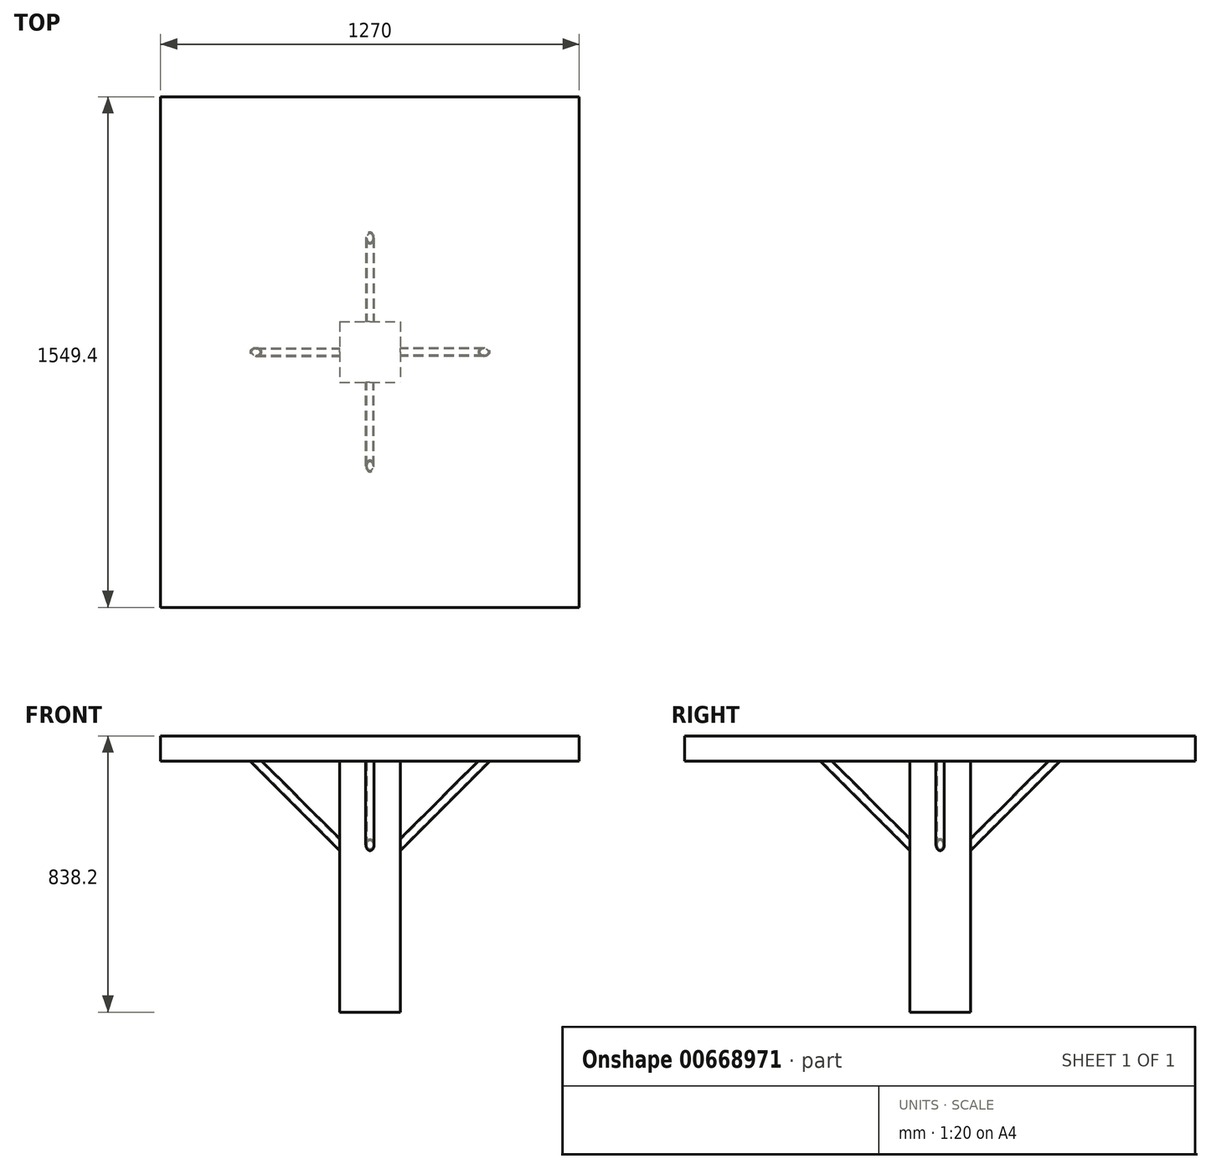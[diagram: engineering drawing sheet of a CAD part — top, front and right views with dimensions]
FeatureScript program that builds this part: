
annotation { "Feature Type Name" : "Feature", "Feature Type Description" : "" }
export const myFeature = defineFeature(function(context is Context, id is Id, definition is map)
    precondition{}
    {
        {
            var Q0;
            Q0=qCreatedBy(makeId("Top.planeOp"),FACE);
            var sketch = newSketch(context, id + "F0", { "sketchPlane" : qUnion([Q0])});
            skLineSegment(sketch, "E0.bottom", {"start": v(-92.08, 92.08) * mm, "end": v(92.08, 92.08) * mm});
            skLineSegment(sketch, "E0.top", {"start": v(-92.08, -92.08) * mm, "end": v(92.08, -92.08) * mm});
            skLineSegment(sketch, "E0.left", {"start": v(-92.08, 92.08) * mm, "end": v(-92.08, -92.08) * mm});
            skLineSegment(sketch, "E0.right", {"start": v(92.08, 92.08) * mm, "end": v(92.08, -92.08) * mm});
            skSolve(sketch);
        }
        {
            var Q0;
            Q0 = qSketchRegion(id + "F0", true);
            extrude(context, id + "F1", {"entities" : qUnion([Q0]), "depth" : 762 * mm, "offsetDistance" : 25.4 * mm});
        }
        {
            var Q0;
            Q0=qCreatedBy(makeId("Front.planeOp"),FACE);
            var sketch = newSketch(context, id + "F2", { "sketchPlane" : qUnion([Q0])});
            skLineSegment(sketch, "E1", {"start": v(0, 1153.25) * mm, "end": v(0, 0) * mm});
            skSolve(sketch);
        }
        {
            var Q0;
            Q0=makeQuery(id+"F1.opExtrude","SWEPT_FACE",FACE,{"disambiguationData":[OSD([sQuery(id+"F0.wireOp",EDGE,"E0.left")])]});
            var sketch = newSketch(context, id + "F3", { "sketchPlane" : qUnion([Q0])});
            skLineSegment(sketch, "E2", {"start": v(92.07, 508) * mm, "end": v(145.96, 561.88) * mm});
            skSolve(sketch);
        }
        {
            var Q0;
            Q0=sQuery(id+"F3.wireOp",VERTEX,"E2.end");
            var Q1;
            Q1=sQuery(id+"F3.wireOp",EDGE,"E2");
            cPlane(context, id + "F4", {"entities" : qUnion([Q0, Q1]), "cplaneType" : CPlaneType.LINE_POINT, "offset" : 25.4 * mm, "width" : 152.4 * mm, "height" : 152.4 * mm});
        }
        {
            var Q0;
            Q0=qCreatedBy(id+"F4.planeOp",FACE);
            var sketch = newSketch(context, id + "F5", { "sketchPlane" : qUnion([Q0])});
            skCircle(sketch, "E3", {"center": v(0, 294.1) * mm, "radius": 12.7 * mm});
            skCircle(sketch, "E4", {"center": v(0, 294.1) * mm, "radius": 9.53 * mm});
            skSolve(sketch);
        }
        {
            var Q0;
            Q0 = qSketchRegion(id + "F5", true);
            extrude(context, id + "F6", {"entities" : qUnion([Q0]), "operationType" : NewBodyOperationType.ADD, "depth" : 355.6 * mm, "offsetDistance" : 25.4 * mm, "hasSecondDirection" : true, "secondDirectionBound" : SecondDirectionBoundingType.UP_TO_NEXT, "secondDirectionOppositeDirection" : true, "secondDirectionDepth" : 25.4 * mm});
        }
        {
            var Q0;
            Q0=makeQuery(id+"F1.opExtrude","SWEPT_BODY",BODY,{"disambiguationData":[OSD([sQuery(id+"F0.wireOp",EDGE,"E0.bottom"),sQuery(id+"F0.wireOp",EDGE,"E0.top"),sQuery(id+"F0.wireOp",EDGE,"E0.left"),sQuery(id+"F0.wireOp",EDGE,"E0.right")])]});
            var Q1;
            Q1=sQuery(id+"F2.wireOp",EDGE,"E1");
            circularPattern(context, id + "F7", {"entities" : qUnion([Q0]), "axis" : qUnion([Q1]), "angle" : 360 * degree, "instanceCount" : 4, "equalSpace" : true});
        }
        {
            var Q0;
            Q0=makeQuery(id+"F1.opExtrude","CAP_FACE",FACE,{"disambiguationData":[OSD([sQuery(id+"F0.wireOp",EDGE,"E0.bottom"),sQuery(id+"F0.wireOp",EDGE,"E0.top"),sQuery(id+"F0.wireOp",EDGE,"E0.left"),sQuery(id+"F0.wireOp",EDGE,"E0.right")])],"isStart":false});
            var sketch = newSketch(context, id + "F8", { "sketchPlane" : qUnion([Q0])});
            skLineSegment(sketch, "E5.bottom", {"start": v(635, 774.7) * mm, "end": v(-635, 774.7) * mm});
            skLineSegment(sketch, "E5.top", {"start": v(635, -774.7) * mm, "end": v(-635, -774.7) * mm});
            skLineSegment(sketch, "E5.left", {"start": v(635, 774.7) * mm, "end": v(635, -774.7) * mm});
            skLineSegment(sketch, "E5.right", {"start": v(-635, 774.7) * mm, "end": v(-635, -774.7) * mm});
            skSolve(sketch);
        }
        {
            var Q0;
            Q0 = qSketchRegion(id + "F8", true);
            extrude(context, id + "F9", {"entities" : qUnion([Q0]), "operationType" : NewBodyOperationType.ADD, "depth" : 76.2 * mm, "offsetDistance" : 25.4 * mm});
        }
    });
